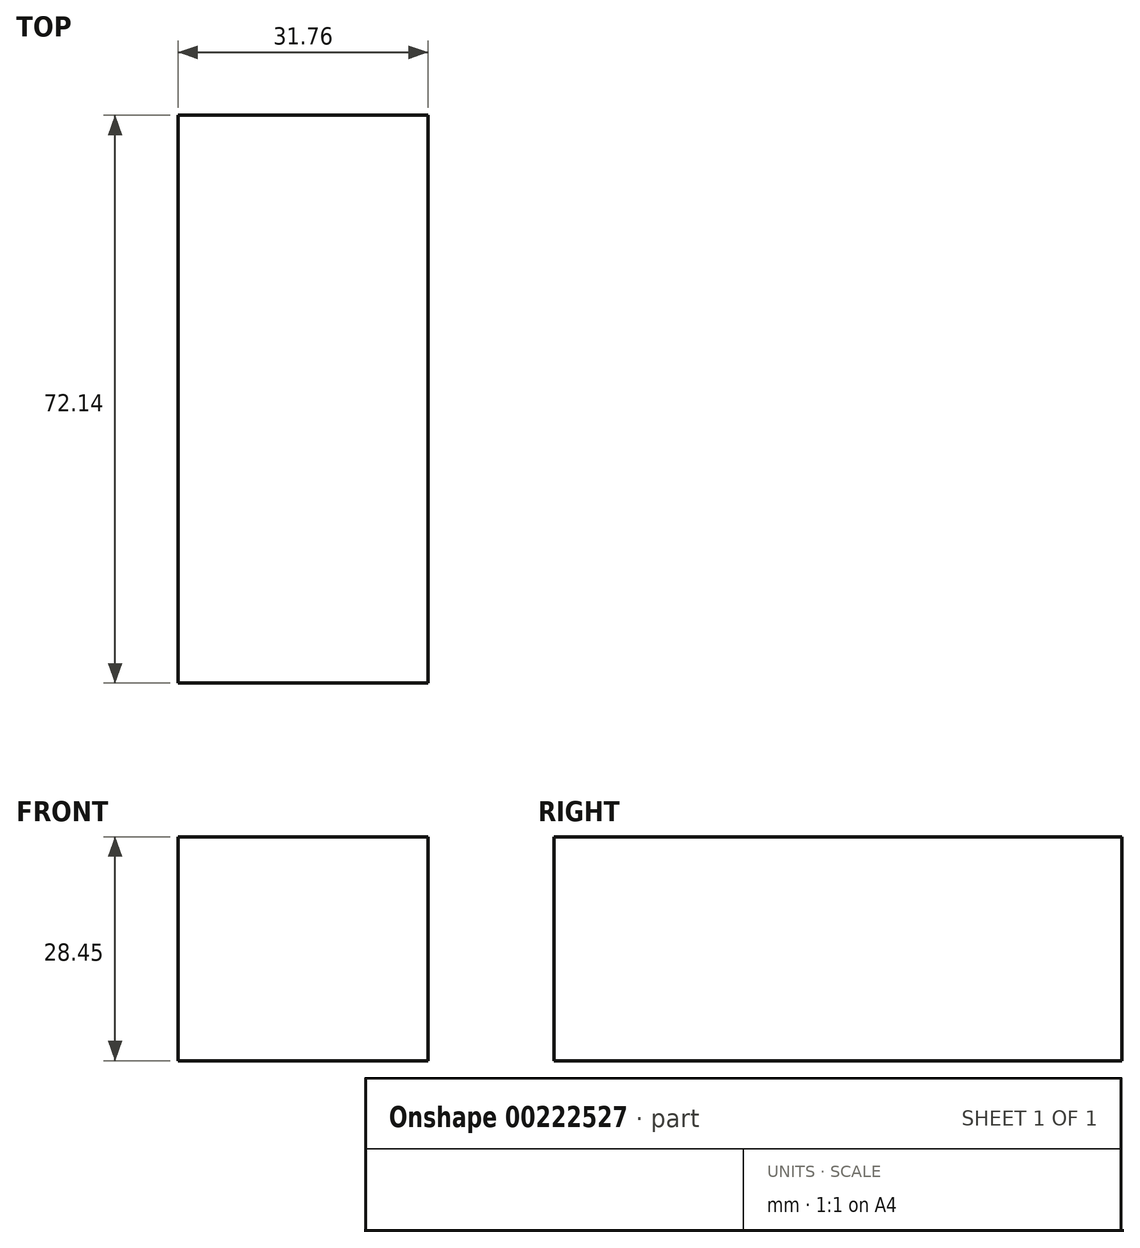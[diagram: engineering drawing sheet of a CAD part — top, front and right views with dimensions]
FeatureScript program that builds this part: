
annotation { "Feature Type Name" : "Feature", "Feature Type Description" : "" }
export const myFeature = defineFeature(function(context is Context, id is Id, definition is map)
    precondition{}
    {
        {
            var Q0;
            Q0=qCreatedBy(makeId("Top.planeOp"),FACE);
            var sketch = newSketch(context, id + "F0", { "sketchPlane" : qUnion([Q0])});
            skLineSegment(sketch, "E0", {"start": v(0, 41.99) * mm, "end": v(15.88, 41.99) * mm});
            skLineSegment(sketch, "E1", {"start": v(0, -30.15) * mm, "end": v(15.88, -30.15) * mm});
            skLineSegment(sketch, "E2", {"start": v(15.87, 41.99) * mm, "end": v(15.88, -30.15) * mm});
            skLineSegment(sketch, "E3", {"start": v(15.88, 41.99) * mm, "end": v(44.45, 41.99) * mm});
            skLineSegment(sketch, "E4", {"start": v(44.45, 41.99) * mm, "end": v(44.45, -62.66) * mm});
            skLineSegment(sketch, "E5", {"start": v(44.45, -62.66) * mm, "end": v(15.88, -34.08) * mm});
            skLineSegment(sketch, "E6", {"start": v(15.88, -34.08) * mm, "end": v(15.88, -30.15) * mm});
            skLineSegment(sketch, "E7", {"start": v(44.45, 35.64) * mm, "end": v(15.88, 35.64) * mm});
            skLineSegment(sketch, "E8", {"start": v(44.45, -27.6) * mm, "end": v(26.92, -27.6) * mm});
            skLineSegment(sketch, "E9", {"start": v(26.92, -27.6) * mm, "end": v(26.92, -45.13) * mm});
            skLineSegment(sketch, "E10.MirrorCS", {"start": v(0, 41.99) * mm, "end": v(-15.88, 41.99) * mm});
            skLineSegment(sketch, "E11.MirrorCS", {"start": v(-15.87, 41.99) * mm, "end": v(-15.88, -30.15) * mm});
            skLineSegment(sketch, "E12.MirrorCS", {"start": v(0, -30.15) * mm, "end": v(-15.88, -30.15) * mm});
            skLineSegment(sketch, "E13.MirrorCS", {"start": v(-15.88, 41.99) * mm, "end": v(-44.45, 41.99) * mm});
            skLineSegment(sketch, "E14.MirrorCS", {"start": v(-44.45, 35.64) * mm, "end": v(-15.88, 35.64) * mm});
            skLineSegment(sketch, "E15.MirrorCS", {"start": v(-44.45, 41.99) * mm, "end": v(-44.45, -62.66) * mm});
            skLineSegment(sketch, "E16.MirrorCS", {"start": v(-44.45, -27.6) * mm, "end": v(-26.92, -27.6) * mm});
            skLineSegment(sketch, "E17.MirrorCS", {"start": v(-26.92, -27.6) * mm, "end": v(-26.92, -45.13) * mm});
            skLineSegment(sketch, "E18.MirrorCS", {"start": v(-44.45, -62.66) * mm, "end": v(-15.88, -34.08) * mm});
            skLineSegment(sketch, "E19.MirrorCS", {"start": v(-15.88, -34.08) * mm, "end": v(-15.88, -30.15) * mm});
            skArc(sketch, "E20", {"start": v(35.75, 13.56) * mm, "mid": v(30.16, 19.15) * mm, "end": v(24.57, 13.56) * mm});
            skPoint(sketch, "E20.centerSnap0", {"position": v(30.16, 35.64) * mm});
            skArc(sketch, "E21", {"start": v(24.57, -10.32) * mm, "mid": v(30.16, -15.9) * mm, "end": v(35.75, -10.32) * mm});
            skLineSegment(sketch, "E22", {"start": v(35.75, 13.56) * mm, "end": v(35.75, -10.32) * mm});
            skLineSegment(sketch, "E23", {"start": v(24.57, 13.56) * mm, "end": v(24.57, -10.32) * mm});
            skArc(sketch, "E24.MirrorC", {"start": v(-35.75, 13.56) * mm, "mid": v(-30.16, 19.15) * mm, "end": v(-24.57, 13.56) * mm});
            skLineSegment(sketch, "E25.MirrorCS", {"start": v(-35.75, 13.56) * mm, "end": v(-35.75, -10.32) * mm});
            skLineSegment(sketch, "E26.MirrorCS", {"start": v(-24.57, 13.56) * mm, "end": v(-24.57, -10.32) * mm});
            skArc(sketch, "E27.MirrorC", {"start": v(-24.57, -10.32) * mm, "mid": v(-30.16, -15.9) * mm, "end": v(-35.75, -10.32) * mm});
            skSolve(sketch);
        }
        {
            var Q0;
            {var subQ3=sQuery(id+"F0.wireOp",EDGE,"E0");Q0=makeQuery(id+"F0.imprint","IMPRINT",FACE,{"disambiguationData":[TD([[makeQuery(id+"F0.imprint","IMPRINT",EDGE,{"derivedFrom":subQ3}),-1.0]])]});}
            extrude(context, id + "F1", {"entities" : qUnion([Q0]), "depth" : 28.45 * mm});
        }
    });
